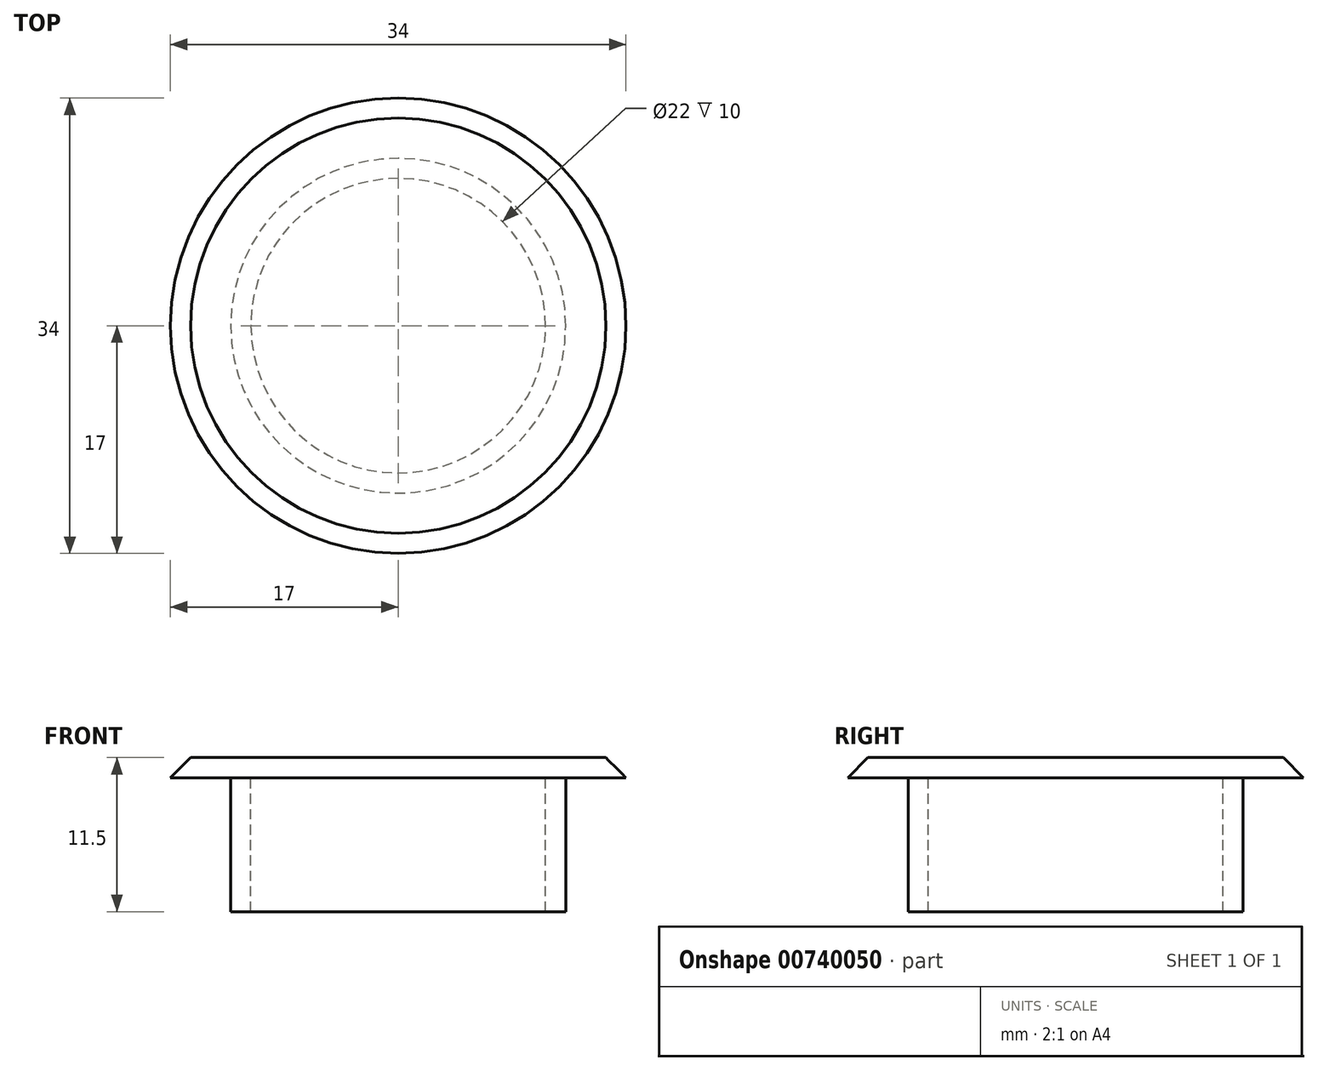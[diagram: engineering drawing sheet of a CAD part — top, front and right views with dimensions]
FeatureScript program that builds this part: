
annotation { "Feature Type Name" : "Feature", "Feature Type Description" : "" }
export const myFeature = defineFeature(function(context is Context, id is Id, definition is map)
    precondition{}
    {
        {
            var Q0;
            Q0=qCreatedBy(makeId("Front.planeOp"),FACE);
            var sketch = newSketch(context, id + "F0", { "sketchPlane" : qUnion([Q0])});
            skLineSegment(sketch, "E0", {"start": v(0, 10) * mm, "end": v(12.5, 10) * mm});
            skLineSegment(sketch, "E1", {"start": v(12.5, 10) * mm, "end": v(12.5, 0) * mm});
            skLineSegment(sketch, "E2", {"start": v(0, 11.5) * mm, "end": v(0, 10) * mm});
            skLineSegment(sketch, "E3", {"start": v(0, 10) * mm, "end": v(17.5, 10) * mm});
            skLineSegment(sketch, "E4", {"start": v(11, 10) * mm, "end": v(11, 0) * mm});
            skLineSegment(sketch, "E5", {"start": v(0, 8.27) * mm, "end": v(11, 8.27) * mm, "construction": true});
            skLineSegment(sketch, "E6", {"start": v(11, 0) * mm, "end": v(12.5, 0) * mm});
            skLineSegment(sketch, "E7", {"start": v(11, 10) * mm, "end": v(12.5, 10) * mm});
            skLineSegment(sketch, "E8", {"start": v(0, 11.5) * mm, "end": v(17.5, 11.5) * mm});
            skLineSegment(sketch, "E9", {"start": v(17.5, 11.5) * mm, "end": v(17.5, 10) * mm});
            skSolve(sketch);
        }
        {
            var Q0;
            {var subQ3=sQuery(id+"F0.wireOp",EDGE,"E2");Q0=makeQuery(id+"F0.imprint","IMPRINT",FACE,{"disambiguationData":[TD([[makeQuery(id+"F0.imprint","IMPRINT",EDGE,{"derivedFrom":subQ3}),1.0]])]});}
            var Q1;
            Q1=makeQuery(id+"F0.imprint","IMPRINT",FACE,{"disambiguationData":[TD([[makeQuery(id+"F0.imprint","IMPRINT",EDGE,{"derivedFrom":sQuery(id+"F0.wireOp",EDGE,"E1")}),-1.0]])]});
            var Q2;
            Q2=sQuery(id+"F0.wireOp",EDGE,"E2");
            revolve(context, id + "F1", {"surfaceOperationType" : NewSurfaceOperationType.NEW, "entities" : qUnion([Q0, Q1]), "axis" : qUnion([Q2]), "revolveType" : RevolveType.FULL});
        }
        {
            var Q0;
            Q0=makeQuery(id+"F1.opRevolve","SWEPT_EDGE",EDGE,{"disambiguationData":[OSD([sQuery(id+"F0.wireOp",EDGE,"E8"),sQuery(id+"F0.wireOp",EDGE,"E9")])]});
            chamfer(context, id + "F2", {"entities" : qUnion([Q0]), "width" : 2 * mm, "tangentPropagation" : true});
        }
    });
